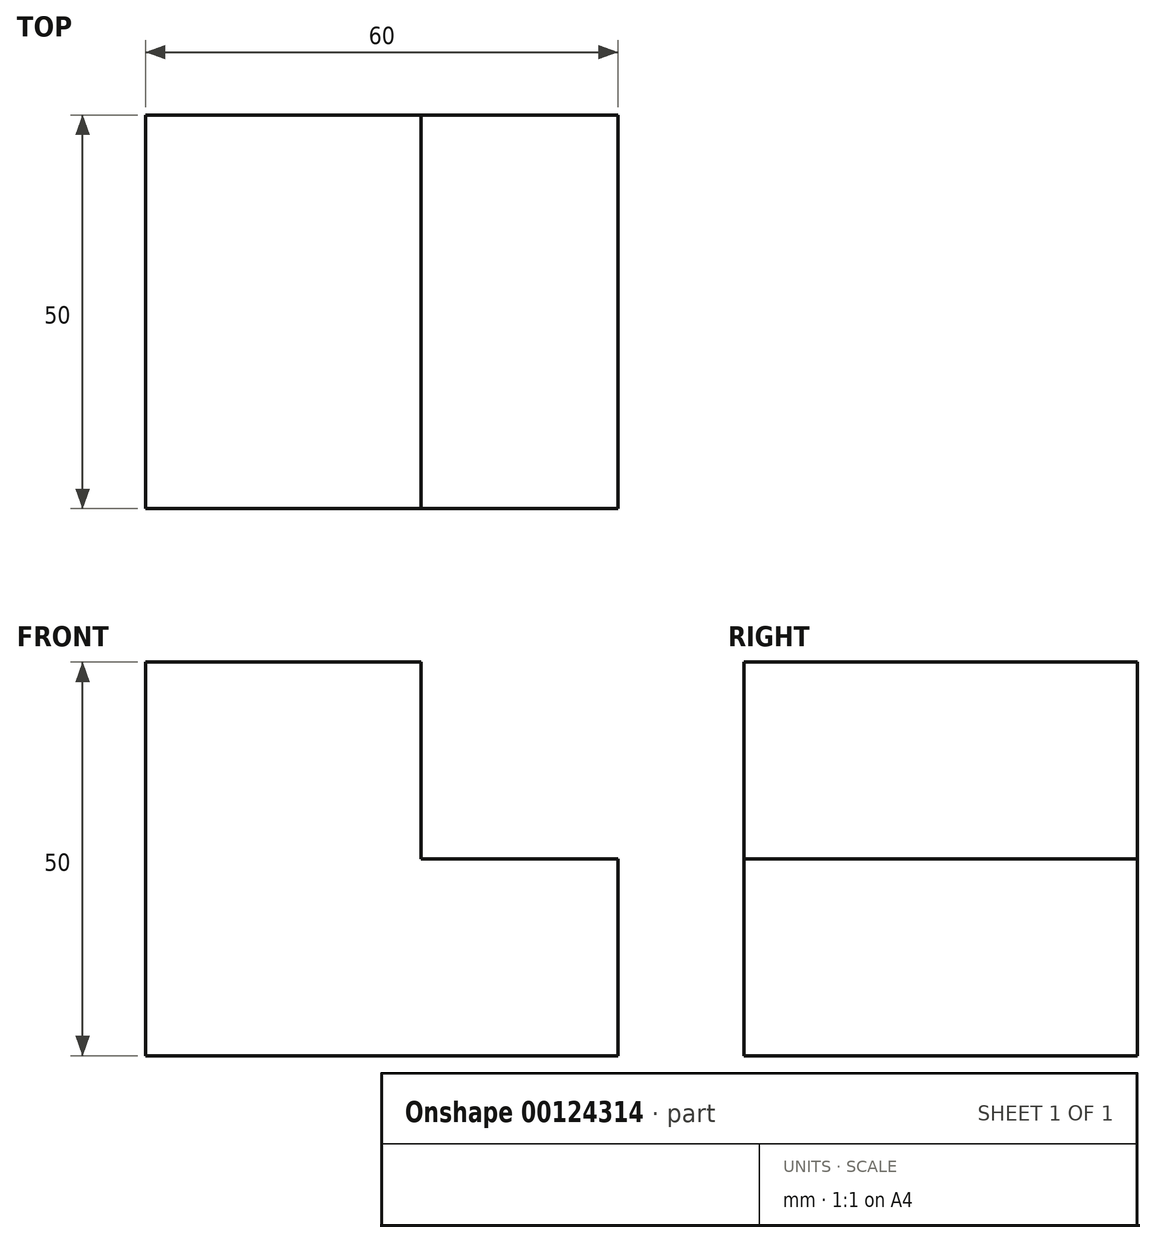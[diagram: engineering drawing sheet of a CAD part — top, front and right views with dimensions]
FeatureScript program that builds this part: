
annotation { "Feature Type Name" : "Feature", "Feature Type Description" : "" }
export const myFeature = defineFeature(function(context is Context, id is Id, definition is map)
    precondition{}
    {
        {
            var Q0;
            Q0=qCreatedBy(makeId("Front.planeOp"),FACE);
            var sketch = newSketch(context, id + "F0", { "sketchPlane" : qUnion([Q0])});
            skLineSegment(sketch, "E0.top", {"start": v(-21.1, -25.53) * mm, "end": v(38.9, -25.53) * mm});
            skLineSegment(sketch, "E0.left", {"start": v(-21.1, 24.47) * mm, "end": v(-21.1, -25.53) * mm});
            skLineSegment(sketch, "E1.top", {"start": v(38.9, -0.53) * mm, "end": v(13.9, -0.53) * mm});
            skLineSegment(sketch, "E1.right", {"start": v(13.9, 24.47) * mm, "end": v(13.9, -0.53) * mm});
            skLineSegment(sketch, "E2", {"start": v(-21.1, 24.47) * mm, "end": v(13.9, 24.47) * mm});
            skLineSegment(sketch, "E3", {"start": v(38.9, -0.53) * mm, "end": v(38.9, -25.53) * mm});
            skSolve(sketch);
        }
        {
            var Q0;
            Q0=makeQuery(id+"F0.imprint","IMPRINT",FACE,{"disambiguationData":[TD([[makeQuery(id+"F0.imprint","IMPRINT",EDGE,{"derivedFrom":sQuery(id+"F0.wireOp",EDGE,"E0.top")}),1.0]])]});
            extrude(context, id + "F1", {"entities" : qUnion([Q0]), "depth" : 50 * mm});
        }
    });
